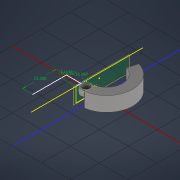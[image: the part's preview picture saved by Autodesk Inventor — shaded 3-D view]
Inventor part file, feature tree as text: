
AUTODESK INVENTOR PART (.ipt)
format: ipt  version: 2021 (Build 250183000, 183)  size: 163,840 bytes
history: native  units: mm
features: sketch x3, extrude x2, plane x2, fillet x2, split x1, other x1
ambient origin geometry x8: Origin, YZ Plane, XZ Plane, XY Plane, X Axis, Y Axis, Z Axis, Center Point
bodies: Solid1 (feature_tree)
feature tree (11):
  extrude  "Extrusion1"  Depth=7.0mm
  plane  "Work Plane1"
  split  "Split1"
  extrude  "Extrusion2"  Depth=10.0mm
  fillet  "Fillet1"  Radius=3.0mm
  fillet  "Fillet2"  Radius=10.0mm
  plane  "Work Plane3"
  sketch  "Sketch5"  dims[d6=0.0mm d7=5.0mm d8=3.0mm d9=10.0mm d10=0.0mm]
  sketch  "Sketch6"  dims[d11=11.0mm d12=0.0mm d14=-2.5mm d15=5.0mm d16=1.0mm d17=0.0mm d21=3.5567mm d22=7.113401mm d23=4.0mm d24=0.0mm d25=0.5mm d26=0.25mm d29=7.113401mm d30=3.5567mm d31=23.308316mm d32=10.096993mm]
  other  "clawBase"
  sketch  "Sketch3"  dims[d3=11.0mm d5=7.0mm]
